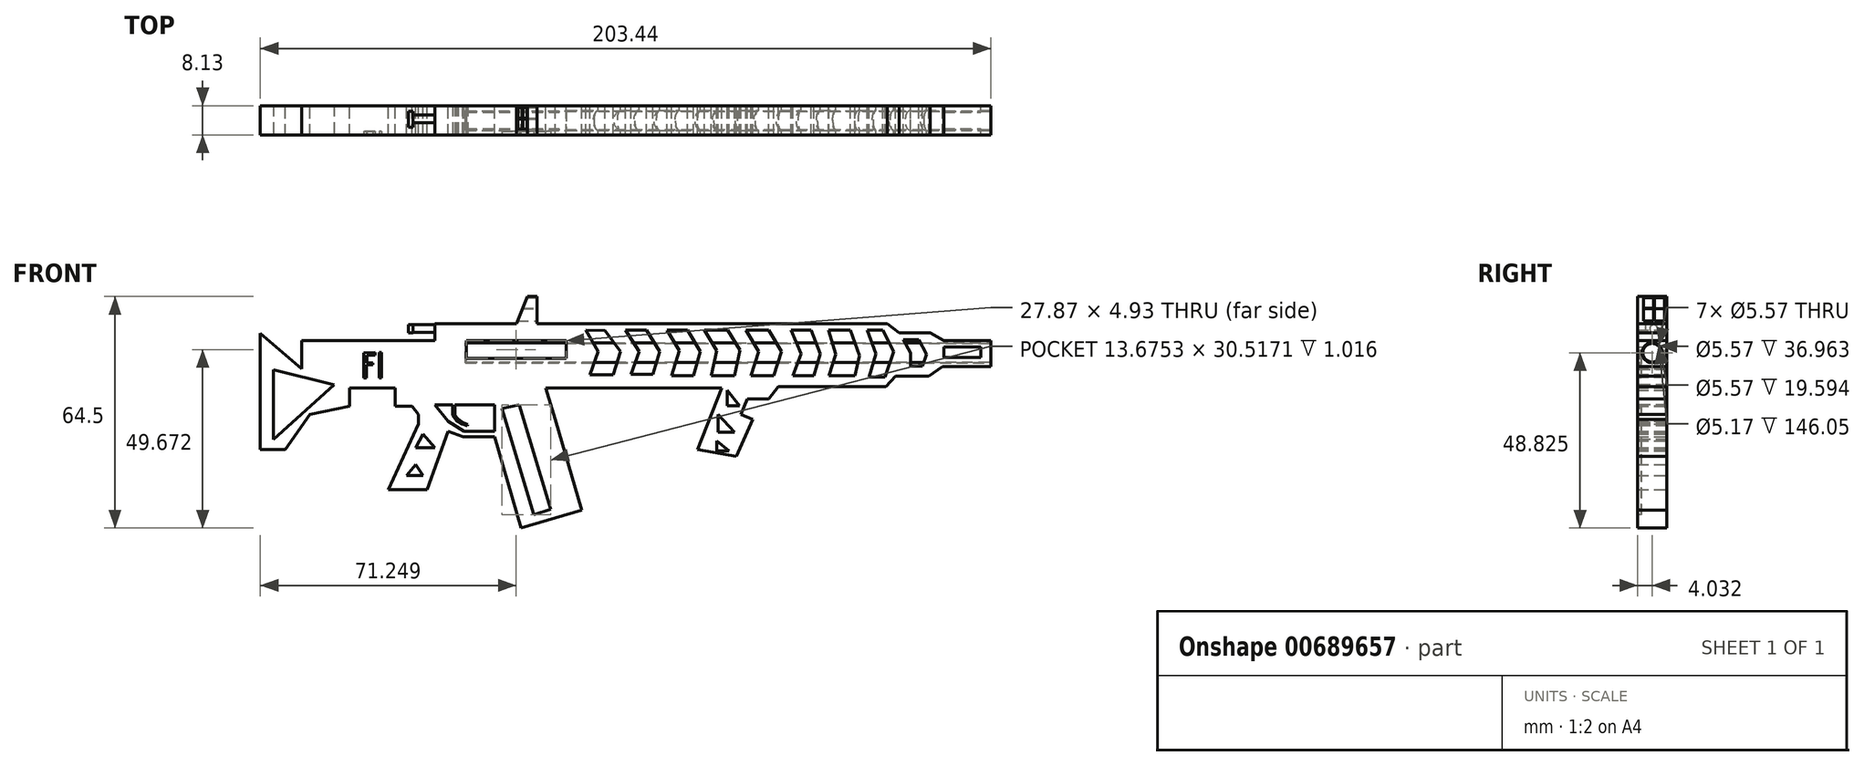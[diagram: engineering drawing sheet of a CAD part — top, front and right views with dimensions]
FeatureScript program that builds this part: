
annotation { "Feature Type Name" : "Feature", "Feature Type Description" : "" }
export const myFeature = defineFeature(function(context is Context, id is Id, definition is map)
    precondition{}
    {
        {
            var Q0;
            Q0=qCreatedBy(makeId("Front.planeOp"),FACE);
            var sketch = newSketch(context, id + "F0", { "sketchPlane" : qUnion([Q0])});
            skLineSegment(sketch, "E0", {"start": v(-48.63, 33.27) * mm, "end": v(-48.63, 11.1) * mm});
            skLineSegment(sketch, "E1", {"start": v(-48.63, 11.1) * mm, "end": v(-41.62, 11.1) * mm});
            skLineSegment(sketch, "E2", {"start": v(-41.62, 11.1) * mm, "end": v(-34.8, 20.95) * mm});
            skLineSegment(sketch, "E3", {"start": v(-34.8, 20.95) * mm, "end": v(-23.8, 23.23) * mm});
            skLineSegment(sketch, "E4", {"start": v(-23.8, 23.23) * mm, "end": v(-23.8, 28.34) * mm});
            skLineSegment(sketch, "E5", {"start": v(-23.8, 28.34) * mm, "end": v(-11.1, 28.34) * mm});
            skLineSegment(sketch, "E6", {"start": v(-11.1, 28.34) * mm, "end": v(-11.1, 23.23) * mm});
            skLineSegment(sketch, "E7", {"start": v(-11.1, 23.23) * mm, "end": v(-6.35, 23.23) * mm});
            skLineSegment(sketch, "E8", {"start": v(-6.35, 23.23) * mm, "end": v(-4.65, 20.95) * mm});
            skLineSegment(sketch, "E9", {"start": v(-4.65, 20.95) * mm, "end": v(-4.65, 18.3) * mm});
            skLineSegment(sketch, "E10", {"start": v(-4.65, 18.3) * mm, "end": v(-12.99, 0) * mm});
            skLineSegment(sketch, "E11", {"start": v(-12.99, 0) * mm, "end": v(-2.18, 0) * mm});
            skLineSegment(sketch, "E12", {"start": v(-2.18, 0) * mm, "end": v(3.7, 16.21) * mm});
            skLineSegment(sketch, "E13", {"start": v(3.7, 16.21) * mm, "end": v(7.92, 14.68) * mm});
            skLineSegment(sketch, "E14", {"start": v(7.92, 14.68) * mm, "end": v(16.59, 14.68) * mm});
            skLineSegment(sketch, "E15", {"start": v(16.59, 14.68) * mm, "end": v(23.98, -10.71) * mm});
            skLineSegment(sketch, "E16", {"start": v(23.98, -10.71) * mm, "end": v(40.91, -5.78) * mm});
            skLineSegment(sketch, "E17", {"start": v(40.91, -5.78) * mm, "end": v(33.55, 19.5) * mm});
            skLineSegment(sketch, "E18", {"start": v(33.55, 19.5) * mm, "end": v(30.8, 28.34) * mm});
            skLineSegment(sketch, "E19", {"start": v(30.8, 28.34) * mm, "end": v(79.92, 28.34) * mm});
            skLineSegment(sketch, "E20", {"start": v(79.92, 28.34) * mm, "end": v(73.09, 11.1) * mm});
            skLineSegment(sketch, "E21", {"start": v(73.09, 11.1) * mm, "end": v(83.9, 9.2) * mm});
            skLineSegment(sketch, "E22", {"start": v(83.9, 9.2) * mm, "end": v(88.45, 19.5) * mm});
            skLineSegment(sketch, "E23", {"start": v(88.45, 19.5) * mm, "end": v(85.15, 20.95) * mm});
            skLineSegment(sketch, "E24", {"start": v(85.15, 20.95) * mm, "end": v(87.03, 25.22) * mm});
            skLineSegment(sketch, "E25", {"start": v(87.03, 25.22) * mm, "end": v(93, 25.22) * mm});
            skLineSegment(sketch, "E26", {"start": v(93, 25.22) * mm, "end": v(95.65, 28.72) * mm});
            skLineSegment(sketch, "E27", {"start": v(95.65, 28.72) * mm, "end": v(125.6, 28.72) * mm});
            skLineSegment(sketch, "E28", {"start": v(125.6, 28.72) * mm, "end": v(128.26, 31.57) * mm});
            skLineSegment(sketch, "E29", {"start": v(128.26, 31.57) * mm, "end": v(137.55, 31.57) * mm});
            skLineSegment(sketch, "E30", {"start": v(137.55, 31.57) * mm, "end": v(141.34, 34.22) * mm});
            skLineSegment(sketch, "E31", {"start": v(141.34, 34.22) * mm, "end": v(154.8, 34.22) * mm});
            skLineSegment(sketch, "E32", {"start": v(154.8, 34.22) * mm, "end": v(154.8, 39.34) * mm});
            skLineSegment(sketch, "E33", {"start": v(154.8, 39.34) * mm, "end": v(154.8, 41.43) * mm});
            skLineSegment(sketch, "E34", {"start": v(154.8, 41.43) * mm, "end": v(141.72, 41.43) * mm});
            skLineSegment(sketch, "E35", {"start": v(141.72, 41.43) * mm, "end": v(137.93, 43.7) * mm});
            skLineSegment(sketch, "E36", {"start": v(137.93, 43.7) * mm, "end": v(129.21, 43.7) * mm});
            skLineSegment(sketch, "E37", {"start": v(129.21, 43.7) * mm, "end": v(125.92, 46.17) * mm});
            skLineSegment(sketch, "E38", {"start": v(125.92, 46.17) * mm, "end": v(0, 46.17) * mm});
            skLineSegment(sketch, "E39", {"start": v(0, 46.17) * mm, "end": v(0, 41.43) * mm});
            skLineSegment(sketch, "E40", {"start": v(0, 41.43) * mm, "end": v(-37.07, 41.43) * mm});
            skLineSegment(sketch, "E41", {"start": v(-37.07, 41.43) * mm, "end": v(-37.07, 33.65) * mm});
            skLineSegment(sketch, "E42", {"start": v(-48.63, 33.27) * mm, "end": v(-48.63, 43.51) * mm});
            skLineSegment(sketch, "E43", {"start": v(-48.63, 43.51) * mm, "end": v(-37.07, 33.65) * mm});
            skLineSegment(sketch, "E44", {"start": v(-3.32, 15.45) * mm, "end": v(-5.4, 11.66) * mm});
            skLineSegment(sketch, "E45", {"start": v(-5.4, 11.66) * mm, "end": v(0, 11.66) * mm});
            skLineSegment(sketch, "E46", {"start": v(0, 11.66) * mm, "end": v(-3.32, 15.45) * mm});
            skLineSegment(sketch, "E47", {"start": v(-5.4, 6.92) * mm, "end": v(-7.87, 3.89) * mm});
            skLineSegment(sketch, "E48", {"start": v(-7.87, 3.89) * mm, "end": v(-3.32, 3.89) * mm});
            skLineSegment(sketch, "E49", {"start": v(-3.32, 3.89) * mm, "end": v(-5.4, 6.92) * mm});
            skLineSegment(sketch, "E50", {"start": v(3.7, 19.05) * mm, "end": v(8.06, 16.21) * mm});
            skLineSegment(sketch, "E51", {"start": v(8.06, 16.21) * mm, "end": v(16.59, 16.21) * mm});
            skLineSegment(sketch, "E52", {"start": v(16.59, 16.21) * mm, "end": v(16.59, 23.6) * mm});
            skLineSegment(sketch, "E53", {"start": v(16.59, 23.6) * mm, "end": v(0, 23.6) * mm});
            skLineSegment(sketch, "E54", {"start": v(0, 23.6) * mm, "end": v(3.7, 19.05) * mm});
            skLineSegment(sketch, "E55", {"start": v(6.35, 23.6) * mm, "end": v(6.35, 20.95) * mm});
            skLineSegment(sketch, "E56", {"start": v(6.35, 20.95) * mm, "end": v(7.68, 19.05) * mm});
            skLineSegment(sketch, "E57", {"start": v(7.68, 19.05) * mm, "end": v(9.32, 17.46) * mm});
            skLineSegment(sketch, "E58", {"start": v(9.32, 17.46) * mm, "end": v(9.77, 17.92) * mm});
            skLineSegment(sketch, "E59", {"start": v(9.77, 17.92) * mm, "end": v(8.6, 19.05) * mm});
            skLineSegment(sketch, "E60", {"start": v(8.6, 19.05) * mm, "end": v(7.08, 20.95) * mm});
            skLineSegment(sketch, "E61", {"start": v(7.08, 20.95) * mm, "end": v(7.08, 23.6) * mm});
            skLineSegment(sketch, "E62", {"start": v(7.08, 23.6) * mm, "end": v(6.35, 23.6) * mm});
            skLineSegment(sketch, "E63", {"start": v(42.05, 44.46) * mm, "end": v(45.46, 38.4) * mm});
            skLineSegment(sketch, "E64", {"start": v(45.46, 38.4) * mm, "end": v(43.19, 31.95) * mm});
            skLineSegment(sketch, "E65", {"start": v(43.19, 31.95) * mm, "end": v(49.64, 31.95) * mm});
            skLineSegment(sketch, "E66", {"start": v(49.64, 31.95) * mm, "end": v(51.72, 38.4) * mm});
            skLineSegment(sketch, "E67", {"start": v(51.72, 38.4) * mm, "end": v(47.36, 44.27) * mm});
            skLineSegment(sketch, "E68", {"start": v(47.36, 44.27) * mm, "end": v(42.05, 44.46) * mm});
            skLineSegment(sketch, "E69", {"start": v(53.05, 44.46) * mm, "end": v(56.84, 38.4) * mm});
            skLineSegment(sketch, "E70", {"start": v(56.84, 38.4) * mm, "end": v(54.57, 32.14) * mm});
            skLineSegment(sketch, "E71", {"start": v(54.57, 32.14) * mm, "end": v(60.63, 32.14) * mm});
            skLineSegment(sketch, "E72", {"start": v(60.63, 32.14) * mm, "end": v(62.53, 38.4) * mm});
            skLineSegment(sketch, "E73", {"start": v(62.53, 38.4) * mm, "end": v(58.93, 44.46) * mm});
            skLineSegment(sketch, "E74", {"start": v(58.93, 44.46) * mm, "end": v(53.05, 44.46) * mm});
            skLineSegment(sketch, "E75", {"start": v(64.61, 44.46) * mm, "end": v(68.07, 38.64) * mm});
            skLineSegment(sketch, "E76", {"start": v(68.07, 38.64) * mm, "end": v(65.94, 31.76) * mm});
            skLineSegment(sketch, "E77", {"start": v(65.94, 31.76) * mm, "end": v(72, 31.76) * mm});
            skLineSegment(sketch, "E78", {"start": v(72, 31.76) * mm, "end": v(73.9, 38.4) * mm});
            skLineSegment(sketch, "E79", {"start": v(73.9, 38.4) * mm, "end": v(70.3, 44.46) * mm});
            skLineSegment(sketch, "E80", {"start": v(70.3, 44.46) * mm, "end": v(64.61, 44.46) * mm});
            skLineSegment(sketch, "E81", {"start": v(75.04, 44.46) * mm, "end": v(78.5, 38.64) * mm});
            skLineSegment(sketch, "E82", {"start": v(78.5, 38.64) * mm, "end": v(76.94, 31.76) * mm});
            skLineSegment(sketch, "E83", {"start": v(76.94, 31.76) * mm, "end": v(83.38, 31.76) * mm});
            skLineSegment(sketch, "E84", {"start": v(83.38, 31.76) * mm, "end": v(84.9, 38.77) * mm});
            skLineSegment(sketch, "E85", {"start": v(84.9, 38.77) * mm, "end": v(81.52, 44.46) * mm});
            skLineSegment(sketch, "E86", {"start": v(75.04, 44.46) * mm, "end": v(81.52, 44.46) * mm});
            skLineSegment(sketch, "E87", {"start": v(86.6, 44.46) * mm, "end": v(90.2, 38.4) * mm});
            skLineSegment(sketch, "E88", {"start": v(90.2, 38.4) * mm, "end": v(88.03, 31.66) * mm});
            skLineSegment(sketch, "E89", {"start": v(88.03, 31.66) * mm, "end": v(94.38, 31.66) * mm});
            skLineSegment(sketch, "E90", {"start": v(94.38, 31.66) * mm, "end": v(96.56, 38.4) * mm});
            skLineSegment(sketch, "E91", {"start": v(96.56, 38.4) * mm, "end": v(92.96, 44.46) * mm});
            skLineSegment(sketch, "E92", {"start": v(92.96, 44.46) * mm, "end": v(86.6, 44.46) * mm});
            skLineSegment(sketch, "E93", {"start": v(99.69, 31.66) * mm, "end": v(101.96, 37.82) * mm});
            skLineSegment(sketch, "E94", {"start": v(101.96, 37.82) * mm, "end": v(99.12, 44.46) * mm});
            skLineSegment(sketch, "E95", {"start": v(99.12, 44.46) * mm, "end": v(104.8, 44.46) * mm});
            skLineSegment(sketch, "E96", {"start": v(104.8, 44.46) * mm, "end": v(107.27, 37.82) * mm});
            skLineSegment(sketch, "E97", {"start": v(107.27, 37.82) * mm, "end": v(105.57, 31.66) * mm});
            skLineSegment(sketch, "E98", {"start": v(105.57, 31.66) * mm, "end": v(99.69, 31.66) * mm});
            skLineSegment(sketch, "E99", {"start": v(109.55, 44.46) * mm, "end": v(111.63, 37.64) * mm});
            skLineSegment(sketch, "E100", {"start": v(111.63, 37.64) * mm, "end": v(109.74, 31.66) * mm});
            skLineSegment(sketch, "E101", {"start": v(109.74, 31.66) * mm, "end": v(116.94, 31.66) * mm});
            skLineSegment(sketch, "E102", {"start": v(116.94, 31.66) * mm, "end": v(118.27, 37.26) * mm});
            skLineSegment(sketch, "E103", {"start": v(118.27, 37.26) * mm, "end": v(115.62, 44.46) * mm});
            skLineSegment(sketch, "E104", {"start": v(115.62, 44.46) * mm, "end": v(109.55, 44.46) * mm});
            skLineSegment(sketch, "E105", {"start": v(120.36, 44.46) * mm, "end": v(122.82, 37.82) * mm});
            skPoint(sketch, "E105.startSnap0", {"position": v(112.58, 44.46) * mm});
            skLineSegment(sketch, "E106", {"start": v(122.82, 37.82) * mm, "end": v(120.92, 31.38) * mm});
            skLineSegment(sketch, "E107", {"start": v(120.92, 31.38) * mm, "end": v(125.29, 31.38) * mm});
            skLineSegment(sketch, "E108", {"start": v(125.29, 31.38) * mm, "end": v(127.75, 38.4) * mm});
            skLineSegment(sketch, "E109", {"start": v(127.75, 38.4) * mm, "end": v(124.72, 44.46) * mm});
            skLineSegment(sketch, "E110", {"start": v(124.72, 44.46) * mm, "end": v(120.36, 44.46) * mm});
            skLineSegment(sketch, "E111", {"start": v(130.4, 41.8) * mm, "end": v(132.5, 38.01) * mm});
            skLineSegment(sketch, "E112", {"start": v(132.5, 38.01) * mm, "end": v(132.5, 34.41) * mm});
            skLineSegment(sketch, "E113", {"start": v(132.5, 34.41) * mm, "end": v(135.78, 34.41) * mm});
            skLineSegment(sketch, "E114", {"start": v(135.78, 34.41) * mm, "end": v(136.85, 37.64) * mm});
            skLineSegment(sketch, "E115", {"start": v(136.85, 37.64) * mm, "end": v(134.77, 41.8) * mm});
            skLineSegment(sketch, "E116", {"start": v(134.77, 41.8) * mm, "end": v(130.4, 41.8) * mm});
            skLineSegment(sketch, "E117", {"start": v(141.72, 39.72) * mm, "end": v(141.72, 36.78) * mm});
            skPoint(sketch, "E117.endSnap0", {"position": v(154.8, 36.78) * mm});
            skLineSegment(sketch, "E118", {"start": v(141.72, 36.78) * mm, "end": v(152.02, 36.78) * mm});
            skLineSegment(sketch, "E119", {"start": v(152.02, 36.78) * mm, "end": v(152.02, 39.72) * mm});
            skLineSegment(sketch, "E120", {"start": v(152.02, 39.72) * mm, "end": v(141.72, 39.72) * mm});
            skLineSegment(sketch, "E121.bottom", {"start": v(8.68, 41.43) * mm, "end": v(36.55, 41.43) * mm});
            skLineSegment(sketch, "E121.top", {"start": v(8.68, 36.5) * mm, "end": v(36.55, 36.5) * mm});
            skLineSegment(sketch, "E121.left", {"start": v(8.68, 41.43) * mm, "end": v(8.68, 36.5) * mm});
            skLineSegment(sketch, "E121.right", {"start": v(36.55, 41.43) * mm, "end": v(36.55, 36.5) * mm});
            skLineSegment(sketch, "E122", {"start": v(78.83, 20.95) * mm, "end": v(78.83, 16.02) * mm});
            skLineSegment(sketch, "E123", {"start": v(78.83, 16.02) * mm, "end": v(83.38, 16.02) * mm});
            skLineSegment(sketch, "E124", {"start": v(83.38, 16.02) * mm, "end": v(78.83, 20.95) * mm});
            skLineSegment(sketch, "E125", {"start": v(78.5, 13.56) * mm, "end": v(78.5, 10.71) * mm});
            skPoint(sketch, "E125.startSnap0", {"position": v(78.5, 10.14) * mm});
            skLineSegment(sketch, "E126", {"start": v(78.5, 10.71) * mm, "end": v(81.9, 10.71) * mm});
            skLineSegment(sketch, "E127", {"start": v(81.9, 10.71) * mm, "end": v(78.5, 13.56) * mm});
            skLineSegment(sketch, "E128", {"start": v(81.34, 27.67) * mm, "end": v(81.34, 23.31) * mm});
            skLineSegment(sketch, "E129", {"start": v(81.34, 23.31) * mm, "end": v(84.86, 23.31) * mm});
            skLineSegment(sketch, "E130", {"start": v(84.86, 23.31) * mm, "end": v(81.34, 27.67) * mm});
            skSolve(sketch);
        }
        {
            var Q0;
            Q0=makeQuery(id+"F0.imprint","IMPRINT",FACE,{"disambiguationData":[TD([[makeQuery(id+"F0.imprint","IMPRINT",EDGE,{"derivedFrom":sQuery(id+"F0.wireOp",EDGE,"E0")}),1.0]])]});
            extrude(context, id + "F1", {"entities" : qUnion([Q0]), "depth" : 7.62 * mm, "offsetDistance" : 25.4 * mm});
        }
        {
            var Q0;
            Q0=makeQuery(id+"F1.opExtrude","SWEPT_FACE",FACE,{"disambiguationData":[OSD([sQuery(id+"F0.wireOp",EDGE,"E32"),sQuery(id+"F0.wireOp",EDGE,"E33")])]});
            var sketch = newSketch(context, id + "F2", { "sketchPlane" : qUnion([Q0])});
            skCircle(sketch, "E131", {"center": v(-4.1, 38.11) * mm, "radius": 2.79 * mm});
            skSolve(sketch);
        }
        {
            var Q0;
            Q0 = qSketchRegion(id + "F2", true);
            extrude(context, id + "F3", {"entities" : qUnion([Q0]), "operationType" : NewBodyOperationType.REMOVE, "oppositeDirection" : true, "depth" : 146.3 * mm, "offsetDistance" : 25.4 * mm});
        }
        {
            var Q0;
            Q0=makeQuery(id+"F1.opExtrude","SWEPT_FACE",FACE,{"disambiguationData":[OSD([sQuery(id+"F0.wireOp",EDGE,"E32"),sQuery(id+"F0.wireOp",EDGE,"E33")])]});
            var sketch = newSketch(context, id + "F4", { "sketchPlane" : qUnion([Q0])});
            skCircle(sketch, "E132", {"center": v(-4.1, 38.11) * mm, "radius": 2.72 * mm});
            skSolve(sketch);
        }
        {
            var Q0;
            Q0 = qSketchRegion(id + "F4", true);
            extrude(context, id + "F5", {"entities" : qUnion([Q0]), "operationType" : NewBodyOperationType.ADD, "oppositeDirection" : true, "depth" : 146.8 * mm, "offsetDistance" : 25.4 * mm});
        }
        {
            var Q0;
            Q0=makeQuery(id+"F5.opExtrude","CAP_FACE",FACE,{"disambiguationData":[OSD([sQuery(id+"F4.wireOp",EDGE,"E132")])],"isStart":true});
            var sketch = newSketch(context, id + "F6", { "sketchPlane" : qUnion([Q0])});
            skCircle(sketch, "E133", {"center": v(-4.1, 38.11) * mm, "radius": 2.59 * mm});
            skSolve(sketch);
        }
        {
            var Q0;
            Q0 = qSketchRegion(id + "F6", true);
            extrude(context, id + "F7", {"entities" : qUnion([Q0]), "operationType" : NewBodyOperationType.REMOVE, "oppositeDirection" : true, "depth" : 146.05 * mm, "offsetDistance" : 25.4 * mm});
        }
        {
            var Q0;
            Q0=makeQuery(id+"F1.opExtrude","SWEPT_FACE",FACE,{"disambiguationData":[OSD([sQuery(id+"F0.wireOp",EDGE,"E38")])]});
            var sketch = newSketch(context, id + "F8", { "sketchPlane" : qUnion([Q0])});
            skLineSegment(sketch, "E134", {"start": v(15.89, 0) * mm, "end": v(15.89, -7.62) * mm});
            skLineSegment(sketch, "E135", {"start": v(15.89, -7.62) * mm, "end": v(28.4, -7.62) * mm});
            skLineSegment(sketch, "E136", {"start": v(28.4, -7.62) * mm, "end": v(28.4, 0) * mm});
            skLineSegment(sketch, "E137", {"start": v(28.4, 0) * mm, "end": v(15.89, 0) * mm});
            skSolve(sketch);
        }
        {
            var Q0;
            Q0 = qSketchRegion(id + "F8", true);
            extrude(context, id + "F9", {"entities" : qUnion([Q0]), "operationType" : NewBodyOperationType.ADD, "depth" : 7.62 * mm, "offsetDistance" : 25.4 * mm});
        }
        {
            var Q0;
            Q0=makeQuery(id+"F9.boolean.opBoolean","MERGE",FACE,{"derivedFrom":[makeQuery(id+"F1.opExtrude","CAP_FACE",FACE,{"disambiguationData":[OSD([sQuery(id+"F0.wireOp",EDGE,"E0"),sQuery(id+"F0.wireOp",EDGE,"E1"),sQuery(id+"F0.wireOp",EDGE,"E2"),sQuery(id+"F0.wireOp",EDGE,"E3"),sQuery(id+"F0.wireOp",EDGE,"E4"),sQuery(id+"F0.wireOp",EDGE,"E5"),sQuery(id+"F0.wireOp",EDGE,"E6"),sQuery(id+"F0.wireOp",EDGE,"E7"),sQuery(id+"F0.wireOp",EDGE,"E8"),sQuery(id+"F0.wireOp",EDGE,"E9"),sQuery(id+"F0.wireOp",EDGE,"E10"),sQuery(id+"F0.wireOp",EDGE,"E11"),sQuery(id+"F0.wireOp",EDGE,"E12"),sQuery(id+"F0.wireOp",EDGE,"E13"),sQuery(id+"F0.wireOp",EDGE,"E14"),sQuery(id+"F0.wireOp",EDGE,"E15"),sQuery(id+"F0.wireOp",EDGE,"E16"),sQuery(id+"F0.wireOp",EDGE,"E17"),sQuery(id+"F0.wireOp",EDGE,"E18"),sQuery(id+"F0.wireOp",EDGE,"E19"),sQuery(id+"F0.wireOp",EDGE,"E20"),sQuery(id+"F0.wireOp",EDGE,"E21"),sQuery(id+"F0.wireOp",EDGE,"E22"),sQuery(id+"F0.wireOp",EDGE,"E23"),sQuery(id+"F0.wireOp",EDGE,"E24"),sQuery(id+"F0.wireOp",EDGE,"E25"),sQuery(id+"F0.wireOp",EDGE,"E26"),sQuery(id+"F0.wireOp",EDGE,"E27"),sQuery(id+"F0.wireOp",EDGE,"E28"),sQuery(id+"F0.wireOp",EDGE,"E29"),sQuery(id+"F0.wireOp",EDGE,"E30"),sQuery(id+"F0.wireOp",EDGE,"E31"),sQuery(id+"F0.wireOp",EDGE,"E32"),sQuery(id+"F0.wireOp",EDGE,"E33"),sQuery(id+"F0.wireOp",EDGE,"E34"),sQuery(id+"F0.wireOp",EDGE,"E35"),sQuery(id+"F0.wireOp",EDGE,"E36"),sQuery(id+"F0.wireOp",EDGE,"E37"),sQuery(id+"F0.wireOp",EDGE,"E38"),sQuery(id+"F0.wireOp",EDGE,"E39"),sQuery(id+"F0.wireOp",EDGE,"E40"),sQuery(id+"F0.wireOp",EDGE,"E41"),sQuery(id+"F0.wireOp",EDGE,"E42"),sQuery(id+"F0.wireOp",EDGE,"E43"),sQuery(id+"F0.wireOp",EDGE,"E44"),sQuery(id+"F0.wireOp",EDGE,"E45"),sQuery(id+"F0.wireOp",EDGE,"E46"),sQuery(id+"F0.wireOp",EDGE,"E47"),sQuery(id+"F0.wireOp",EDGE,"E48"),sQuery(id+"F0.wireOp",EDGE,"E49"),sQuery(id+"F0.wireOp",EDGE,"E50"),sQuery(id+"F0.wireOp",EDGE,"E51"),sQuery(id+"F0.wireOp",EDGE,"E52"),sQuery(id+"F0.wireOp",EDGE,"E53"),sQuery(id+"F0.wireOp",EDGE,"E54"),sQuery(id+"F0.wireOp",EDGE,"E62"),sQuery(id+"F0.wireOp",EDGE,"E63"),sQuery(id+"F0.wireOp",EDGE,"E64"),sQuery(id+"F0.wireOp",EDGE,"E65"),sQuery(id+"F0.wireOp",EDGE,"E66"),sQuery(id+"F0.wireOp",EDGE,"E67"),sQuery(id+"F0.wireOp",EDGE,"E68"),sQuery(id+"F0.wireOp",EDGE,"E69"),sQuery(id+"F0.wireOp",EDGE,"E70"),sQuery(id+"F0.wireOp",EDGE,"E71"),sQuery(id+"F0.wireOp",EDGE,"E72"),sQuery(id+"F0.wireOp",EDGE,"E73"),sQuery(id+"F0.wireOp",EDGE,"E74"),sQuery(id+"F0.wireOp",EDGE,"E75"),sQuery(id+"F0.wireOp",EDGE,"E76"),sQuery(id+"F0.wireOp",EDGE,"E77"),sQuery(id+"F0.wireOp",EDGE,"E78"),sQuery(id+"F0.wireOp",EDGE,"E79"),sQuery(id+"F0.wireOp",EDGE,"E80"),sQuery(id+"F0.wireOp",EDGE,"E81"),sQuery(id+"F0.wireOp",EDGE,"E82"),sQuery(id+"F0.wireOp",EDGE,"E83"),sQuery(id+"F0.wireOp",EDGE,"E84"),sQuery(id+"F0.wireOp",EDGE,"E85"),sQuery(id+"F0.wireOp",EDGE,"E86"),sQuery(id+"F0.wireOp",EDGE,"E87"),sQuery(id+"F0.wireOp",EDGE,"E88"),sQuery(id+"F0.wireOp",EDGE,"E89"),sQuery(id+"F0.wireOp",EDGE,"E90"),sQuery(id+"F0.wireOp",EDGE,"E91"),sQuery(id+"F0.wireOp",EDGE,"E92"),sQuery(id+"F0.wireOp",EDGE,"E93"),sQuery(id+"F0.wireOp",EDGE,"E94"),sQuery(id+"F0.wireOp",EDGE,"E95"),sQuery(id+"F0.wireOp",EDGE,"E96"),sQuery(id+"F0.wireOp",EDGE,"E97"),sQuery(id+"F0.wireOp",EDGE,"E98"),sQuery(id+"F0.wireOp",EDGE,"E99"),sQuery(id+"F0.wireOp",EDGE,"E100"),sQuery(id+"F0.wireOp",EDGE,"E101"),sQuery(id+"F0.wireOp",EDGE,"E102"),sQuery(id+"F0.wireOp",EDGE,"E103"),sQuery(id+"F0.wireOp",EDGE,"E104"),sQuery(id+"F0.wireOp",EDGE,"E105"),sQuery(id+"F0.wireOp",EDGE,"E106"),sQuery(id+"F0.wireOp",EDGE,"E107"),sQuery(id+"F0.wireOp",EDGE,"E108"),sQuery(id+"F0.wireOp",EDGE,"E109"),sQuery(id+"F0.wireOp",EDGE,"E110"),sQuery(id+"F0.wireOp",EDGE,"E111"),sQuery(id+"F0.wireOp",EDGE,"E112"),sQuery(id+"F0.wireOp",EDGE,"E113"),sQuery(id+"F0.wireOp",EDGE,"E114"),sQuery(id+"F0.wireOp",EDGE,"E115"),sQuery(id+"F0.wireOp",EDGE,"E116"),sQuery(id+"F0.wireOp",EDGE,"E117"),sQuery(id+"F0.wireOp",EDGE,"E118"),sQuery(id+"F0.wireOp",EDGE,"E119"),sQuery(id+"F0.wireOp",EDGE,"E120"),sQuery(id+"F0.wireOp",EDGE,"E121.bottom"),sQuery(id+"F0.wireOp",EDGE,"E121.top"),sQuery(id+"F0.wireOp",EDGE,"E121.left"),sQuery(id+"F0.wireOp",EDGE,"E121.right"),sQuery(id+"F0.wireOp",EDGE,"E122"),sQuery(id+"F0.wireOp",EDGE,"E123"),sQuery(id+"F0.wireOp",EDGE,"E124"),sQuery(id+"F0.wireOp",EDGE,"E125"),sQuery(id+"F0.wireOp",EDGE,"E126"),sQuery(id+"F0.wireOp",EDGE,"E127"),sQuery(id+"F0.wireOp",EDGE,"E128"),sQuery(id+"F0.wireOp",EDGE,"E129"),sQuery(id+"F0.wireOp",EDGE,"E130")])],"isStart":false}),makeQuery(id+"F9.opExtrude","SWEPT_FACE",FACE,{"disambiguationData":[OSD([sQuery(id+"F8.wireOp",EDGE,"E135")])]})]});
            var sketch = newSketch(context, id + "F10", { "sketchPlane" : qUnion([Q0])});
            skLineSegment(sketch, "E138", {"start": v(15.89, 46.17) * mm, "end": v(22.72, 46.17) * mm});
            skLineSegment(sketch, "E139", {"start": v(22.72, 46.17) * mm, "end": v(25.8, 53.79) * mm});
            skLineSegment(sketch, "E140", {"start": v(25.8, 53.79) * mm, "end": v(15.89, 53.79) * mm});
            skLineSegment(sketch, "E141", {"start": v(15.89, 53.79) * mm, "end": v(15.89, 46.17) * mm});
            skSolve(sketch);
        }
        {
            var Q0;
            Q0 = qSketchRegion(id + "F10", true);
            extrude(context, id + "F11", {"entities" : qUnion([Q0]), "operationType" : NewBodyOperationType.REMOVE, "oppositeDirection" : true, "depth" : 25.4 * mm, "offsetDistance" : 25.4 * mm});
        }
        {
            var Q0;
            Q0=makeQuery(id+"F9.opExtrude","SWEPT_FACE",FACE,{"disambiguationData":[OSD([sQuery(id+"F8.wireOp",EDGE,"E136")])]});
            var sketch = newSketch(context, id + "F12", { "sketchPlane" : qUnion([Q0])});
            skLineSegment(sketch, "E142", {"start": v(-6.51, 53.46) * mm, "end": v(-6.51, 50.45) * mm});
            skLineSegment(sketch, "E143", {"start": v(-6.51, 50.45) * mm, "end": v(-3.67, 50.45) * mm});
            skLineSegment(sketch, "E144", {"start": v(-3.67, 50.45) * mm, "end": v(-3.67, 53.47) * mm});
            skLineSegment(sketch, "E145", {"start": v(-3.67, 53.47) * mm, "end": v(-6.51, 53.46) * mm});
            skLineSegment(sketch, "E146", {"start": v(-3.48, 53.46) * mm, "end": v(-0.59, 53.47) * mm});
            skLineSegment(sketch, "E147", {"start": v(-0.59, 53.47) * mm, "end": v(-0.59, 50.45) * mm});
            skLineSegment(sketch, "E148", {"start": v(-0.59, 50.45) * mm, "end": v(-3.48, 50.43) * mm});
            skLineSegment(sketch, "E149", {"start": v(-3.48, 50.43) * mm, "end": v(-3.48, 53.46) * mm});
            skLineSegment(sketch, "E150", {"start": v(-6.52, 50.32) * mm, "end": v(-6.52, 46.98) * mm});
            skLineSegment(sketch, "E151", {"start": v(-6.52, 46.98) * mm, "end": v(-3.67, 46.98) * mm});
            skLineSegment(sketch, "E152", {"start": v(-3.67, 46.98) * mm, "end": v(-3.67, 50.32) * mm});
            skLineSegment(sketch, "E153", {"start": v(-3.67, 50.32) * mm, "end": v(-6.52, 50.32) * mm});
            skLineSegment(sketch, "E154", {"start": v(-3.48, 50.32) * mm, "end": v(-0.59, 50.32) * mm});
            skLineSegment(sketch, "E155", {"start": v(-0.59, 50.32) * mm, "end": v(-0.59, 46.98) * mm});
            skLineSegment(sketch, "E156", {"start": v(-0.59, 46.98) * mm, "end": v(-3.48, 46.98) * mm});
            skLineSegment(sketch, "E157", {"start": v(-3.48, 46.98) * mm, "end": v(-3.48, 50.32) * mm});
            skSolve(sketch);
        }
        {
            var Q0;
            Q0 = qSketchRegion(id + "F12", true);
            extrude(context, id + "F13", {"entities" : qUnion([Q0]), "operationType" : NewBodyOperationType.REMOVE, "oppositeDirection" : true, "depth" : 25.4 * mm, "offsetDistance" : 25.4 * mm});
        }
        {
            var Q0;
            Q0=makeQuery(id+"F9.boolean.opBoolean","MERGE",FACE,{"derivedFrom":[makeQuery(id+"F1.opExtrude","CAP_FACE",FACE,{"disambiguationData":[OSD([sQuery(id+"F0.wireOp",EDGE,"E0"),sQuery(id+"F0.wireOp",EDGE,"E1"),sQuery(id+"F0.wireOp",EDGE,"E2"),sQuery(id+"F0.wireOp",EDGE,"E3"),sQuery(id+"F0.wireOp",EDGE,"E4"),sQuery(id+"F0.wireOp",EDGE,"E5"),sQuery(id+"F0.wireOp",EDGE,"E6"),sQuery(id+"F0.wireOp",EDGE,"E7"),sQuery(id+"F0.wireOp",EDGE,"E8"),sQuery(id+"F0.wireOp",EDGE,"E9"),sQuery(id+"F0.wireOp",EDGE,"E10"),sQuery(id+"F0.wireOp",EDGE,"E11"),sQuery(id+"F0.wireOp",EDGE,"E12"),sQuery(id+"F0.wireOp",EDGE,"E13"),sQuery(id+"F0.wireOp",EDGE,"E14"),sQuery(id+"F0.wireOp",EDGE,"E15"),sQuery(id+"F0.wireOp",EDGE,"E16"),sQuery(id+"F0.wireOp",EDGE,"E17"),sQuery(id+"F0.wireOp",EDGE,"E18"),sQuery(id+"F0.wireOp",EDGE,"E19"),sQuery(id+"F0.wireOp",EDGE,"E20"),sQuery(id+"F0.wireOp",EDGE,"E21"),sQuery(id+"F0.wireOp",EDGE,"E22"),sQuery(id+"F0.wireOp",EDGE,"E23"),sQuery(id+"F0.wireOp",EDGE,"E24"),sQuery(id+"F0.wireOp",EDGE,"E25"),sQuery(id+"F0.wireOp",EDGE,"E26"),sQuery(id+"F0.wireOp",EDGE,"E27"),sQuery(id+"F0.wireOp",EDGE,"E28"),sQuery(id+"F0.wireOp",EDGE,"E29"),sQuery(id+"F0.wireOp",EDGE,"E30"),sQuery(id+"F0.wireOp",EDGE,"E31"),sQuery(id+"F0.wireOp",EDGE,"E32"),sQuery(id+"F0.wireOp",EDGE,"E33"),sQuery(id+"F0.wireOp",EDGE,"E34"),sQuery(id+"F0.wireOp",EDGE,"E35"),sQuery(id+"F0.wireOp",EDGE,"E36"),sQuery(id+"F0.wireOp",EDGE,"E37"),sQuery(id+"F0.wireOp",EDGE,"E38"),sQuery(id+"F0.wireOp",EDGE,"E39"),sQuery(id+"F0.wireOp",EDGE,"E40"),sQuery(id+"F0.wireOp",EDGE,"E41"),sQuery(id+"F0.wireOp",EDGE,"E42"),sQuery(id+"F0.wireOp",EDGE,"E43"),sQuery(id+"F0.wireOp",EDGE,"E44"),sQuery(id+"F0.wireOp",EDGE,"E45"),sQuery(id+"F0.wireOp",EDGE,"E46"),sQuery(id+"F0.wireOp",EDGE,"E47"),sQuery(id+"F0.wireOp",EDGE,"E48"),sQuery(id+"F0.wireOp",EDGE,"E49"),sQuery(id+"F0.wireOp",EDGE,"E50"),sQuery(id+"F0.wireOp",EDGE,"E51"),sQuery(id+"F0.wireOp",EDGE,"E52"),sQuery(id+"F0.wireOp",EDGE,"E53"),sQuery(id+"F0.wireOp",EDGE,"E54"),sQuery(id+"F0.wireOp",EDGE,"E62"),sQuery(id+"F0.wireOp",EDGE,"E63"),sQuery(id+"F0.wireOp",EDGE,"E64"),sQuery(id+"F0.wireOp",EDGE,"E65"),sQuery(id+"F0.wireOp",EDGE,"E66"),sQuery(id+"F0.wireOp",EDGE,"E67"),sQuery(id+"F0.wireOp",EDGE,"E68"),sQuery(id+"F0.wireOp",EDGE,"E69"),sQuery(id+"F0.wireOp",EDGE,"E70"),sQuery(id+"F0.wireOp",EDGE,"E71"),sQuery(id+"F0.wireOp",EDGE,"E72"),sQuery(id+"F0.wireOp",EDGE,"E73"),sQuery(id+"F0.wireOp",EDGE,"E74"),sQuery(id+"F0.wireOp",EDGE,"E75"),sQuery(id+"F0.wireOp",EDGE,"E76"),sQuery(id+"F0.wireOp",EDGE,"E77"),sQuery(id+"F0.wireOp",EDGE,"E78"),sQuery(id+"F0.wireOp",EDGE,"E79"),sQuery(id+"F0.wireOp",EDGE,"E80"),sQuery(id+"F0.wireOp",EDGE,"E81"),sQuery(id+"F0.wireOp",EDGE,"E82"),sQuery(id+"F0.wireOp",EDGE,"E83"),sQuery(id+"F0.wireOp",EDGE,"E84"),sQuery(id+"F0.wireOp",EDGE,"E85"),sQuery(id+"F0.wireOp",EDGE,"E86"),sQuery(id+"F0.wireOp",EDGE,"E87"),sQuery(id+"F0.wireOp",EDGE,"E88"),sQuery(id+"F0.wireOp",EDGE,"E89"),sQuery(id+"F0.wireOp",EDGE,"E90"),sQuery(id+"F0.wireOp",EDGE,"E91"),sQuery(id+"F0.wireOp",EDGE,"E92"),sQuery(id+"F0.wireOp",EDGE,"E93"),sQuery(id+"F0.wireOp",EDGE,"E94"),sQuery(id+"F0.wireOp",EDGE,"E95"),sQuery(id+"F0.wireOp",EDGE,"E96"),sQuery(id+"F0.wireOp",EDGE,"E97"),sQuery(id+"F0.wireOp",EDGE,"E98"),sQuery(id+"F0.wireOp",EDGE,"E99"),sQuery(id+"F0.wireOp",EDGE,"E100"),sQuery(id+"F0.wireOp",EDGE,"E101"),sQuery(id+"F0.wireOp",EDGE,"E102"),sQuery(id+"F0.wireOp",EDGE,"E103"),sQuery(id+"F0.wireOp",EDGE,"E104"),sQuery(id+"F0.wireOp",EDGE,"E105"),sQuery(id+"F0.wireOp",EDGE,"E106"),sQuery(id+"F0.wireOp",EDGE,"E107"),sQuery(id+"F0.wireOp",EDGE,"E108"),sQuery(id+"F0.wireOp",EDGE,"E109"),sQuery(id+"F0.wireOp",EDGE,"E110"),sQuery(id+"F0.wireOp",EDGE,"E111"),sQuery(id+"F0.wireOp",EDGE,"E112"),sQuery(id+"F0.wireOp",EDGE,"E113"),sQuery(id+"F0.wireOp",EDGE,"E114"),sQuery(id+"F0.wireOp",EDGE,"E115"),sQuery(id+"F0.wireOp",EDGE,"E116"),sQuery(id+"F0.wireOp",EDGE,"E117"),sQuery(id+"F0.wireOp",EDGE,"E118"),sQuery(id+"F0.wireOp",EDGE,"E119"),sQuery(id+"F0.wireOp",EDGE,"E120"),sQuery(id+"F0.wireOp",EDGE,"E121.bottom"),sQuery(id+"F0.wireOp",EDGE,"E121.top"),sQuery(id+"F0.wireOp",EDGE,"E121.left"),sQuery(id+"F0.wireOp",EDGE,"E121.right"),sQuery(id+"F0.wireOp",EDGE,"E122"),sQuery(id+"F0.wireOp",EDGE,"E123"),sQuery(id+"F0.wireOp",EDGE,"E124"),sQuery(id+"F0.wireOp",EDGE,"E125"),sQuery(id+"F0.wireOp",EDGE,"E126"),sQuery(id+"F0.wireOp",EDGE,"E127"),sQuery(id+"F0.wireOp",EDGE,"E128"),sQuery(id+"F0.wireOp",EDGE,"E129"),sQuery(id+"F0.wireOp",EDGE,"E130")])],"isStart":false}),makeQuery(id+"F9.opExtrude","SWEPT_FACE",FACE,{"disambiguationData":[OSD([sQuery(id+"F8.wireOp",EDGE,"E135")])]})]});
            var sketch = newSketch(context, id + "F14", { "sketchPlane" : qUnion([Q0])});
            skLineSegment(sketch, "E158", {"start": v(4.94, 20.64) * mm, "end": v(6, 19.32) * mm});
            skLineSegment(sketch, "E159", {"start": v(6, 19.32) * mm, "end": v(7.62, 18.25) * mm});
            skLineSegment(sketch, "E160", {"start": v(7.62, 18.25) * mm, "end": v(8.96, 17.71) * mm});
            skLineSegment(sketch, "E161", {"start": v(8.96, 17.71) * mm, "end": v(9.12, 18.12) * mm});
            skLineSegment(sketch, "E162", {"start": v(9.12, 18.12) * mm, "end": v(7.87, 18.62) * mm});
            skLineSegment(sketch, "E163", {"start": v(7.87, 18.62) * mm, "end": v(6.48, 19.59) * mm});
            skLineSegment(sketch, "E164", {"start": v(6.48, 19.59) * mm, "end": v(5.54, 20.7) * mm});
            skLineSegment(sketch, "E165", {"start": v(5.54, 20.7) * mm, "end": v(5.54, 23.91) * mm});
            skLineSegment(sketch, "E166", {"start": v(5.54, 23.91) * mm, "end": v(4.97, 23.91) * mm});
            skLineSegment(sketch, "E167", {"start": v(4.94, 20.64) * mm, "end": v(4.97, 23.91) * mm});
            skSolve(sketch);
        }
        {
            var Q0;
            Q0 = qSketchRegion(id + "F14", true);
            extrude(context, id + "F15", {"entities" : qUnion([Q0]), "operationType" : NewBodyOperationType.ADD, "oppositeDirection" : true, "depth" : 7.62 * mm, "offsetDistance" : 25.4 * mm});
        }
        {
            var Q0;
            Q0=makeQuery(id+"F1.opExtrude","SWEPT_FACE",FACE,{"disambiguationData":[OSD([sQuery(id+"F0.wireOp",EDGE,"E39")])]});
            var sketch = newSketch(context, id + "F16", { "sketchPlane" : qUnion([Q0])});
            skCircle(sketch, "E168", {"center": v(3.66, 44.8) * mm, "radius": 1.1 * mm});
            skSolve(sketch);
        }
        {
            var Q0;
            Q0 = qSketchRegion(id + "F16", true);
            extrude(context, id + "F17", {"entities" : qUnion([Q0]), "operationType" : NewBodyOperationType.ADD, "depth" : 6.1 * mm, "offsetDistance" : 25.4 * mm});
        }
        {
            var Q0;
            Q0=makeQuery(id+"F17.opExtrude","CAP_FACE",FACE,{"disambiguationData":[OSD([sQuery(id+"F16.wireOp",EDGE,"E168")])],"isStart":false});
            var sketch = newSketch(context, id + "F18", { "sketchPlane" : qUnion([Q0])});
            skLineSegment(sketch, "E169.bottom", {"start": v(1.57, 45.88) * mm, "end": v(5.98, 45.88) * mm});
            skLineSegment(sketch, "E169.top", {"start": v(1.57, 43.69) * mm, "end": v(5.98, 43.69) * mm});
            skLineSegment(sketch, "E169.left", {"start": v(1.57, 45.88) * mm, "end": v(1.57, 43.69) * mm});
            skLineSegment(sketch, "E169.right", {"start": v(5.98, 45.88) * mm, "end": v(5.98, 43.69) * mm});
            skSolve(sketch);
        }
        {
            var Q0;
            Q0 = qSketchRegion(id + "F18", true);
            extrude(context, id + "F19", {"entities" : qUnion([Q0]), "operationType" : NewBodyOperationType.ADD, "depth" : 1.27 * mm, "offsetDistance" : 25.4 * mm});
        }
        {
            var Q0;
            Q0=makeQuery(id+"F15.boolean.opBoolean","MERGE",FACE,{"derivedFrom":[makeQuery(id+"F9.boolean.opBoolean","MERGE",FACE,{"derivedFrom":[makeQuery(id+"F1.opExtrude","CAP_FACE",FACE,{"disambiguationData":[OSD([sQuery(id+"F0.wireOp",EDGE,"E0"),sQuery(id+"F0.wireOp",EDGE,"E1"),sQuery(id+"F0.wireOp",EDGE,"E2"),sQuery(id+"F0.wireOp",EDGE,"E3"),sQuery(id+"F0.wireOp",EDGE,"E4"),sQuery(id+"F0.wireOp",EDGE,"E5"),sQuery(id+"F0.wireOp",EDGE,"E6"),sQuery(id+"F0.wireOp",EDGE,"E7"),sQuery(id+"F0.wireOp",EDGE,"E8"),sQuery(id+"F0.wireOp",EDGE,"E9"),sQuery(id+"F0.wireOp",EDGE,"E10"),sQuery(id+"F0.wireOp",EDGE,"E11"),sQuery(id+"F0.wireOp",EDGE,"E12"),sQuery(id+"F0.wireOp",EDGE,"E13"),sQuery(id+"F0.wireOp",EDGE,"E14"),sQuery(id+"F0.wireOp",EDGE,"E15"),sQuery(id+"F0.wireOp",EDGE,"E16"),sQuery(id+"F0.wireOp",EDGE,"E17"),sQuery(id+"F0.wireOp",EDGE,"E18"),sQuery(id+"F0.wireOp",EDGE,"E19"),sQuery(id+"F0.wireOp",EDGE,"E20"),sQuery(id+"F0.wireOp",EDGE,"E21"),sQuery(id+"F0.wireOp",EDGE,"E22"),sQuery(id+"F0.wireOp",EDGE,"E23"),sQuery(id+"F0.wireOp",EDGE,"E24"),sQuery(id+"F0.wireOp",EDGE,"E25"),sQuery(id+"F0.wireOp",EDGE,"E26"),sQuery(id+"F0.wireOp",EDGE,"E27"),sQuery(id+"F0.wireOp",EDGE,"E28"),sQuery(id+"F0.wireOp",EDGE,"E29"),sQuery(id+"F0.wireOp",EDGE,"E30"),sQuery(id+"F0.wireOp",EDGE,"E31"),sQuery(id+"F0.wireOp",EDGE,"E32"),sQuery(id+"F0.wireOp",EDGE,"E33"),sQuery(id+"F0.wireOp",EDGE,"E34"),sQuery(id+"F0.wireOp",EDGE,"E35"),sQuery(id+"F0.wireOp",EDGE,"E36"),sQuery(id+"F0.wireOp",EDGE,"E37"),sQuery(id+"F0.wireOp",EDGE,"E38"),sQuery(id+"F0.wireOp",EDGE,"E39"),sQuery(id+"F0.wireOp",EDGE,"E40"),sQuery(id+"F0.wireOp",EDGE,"E41"),sQuery(id+"F0.wireOp",EDGE,"E42"),sQuery(id+"F0.wireOp",EDGE,"E43"),sQuery(id+"F0.wireOp",EDGE,"E44"),sQuery(id+"F0.wireOp",EDGE,"E45"),sQuery(id+"F0.wireOp",EDGE,"E46"),sQuery(id+"F0.wireOp",EDGE,"E47"),sQuery(id+"F0.wireOp",EDGE,"E48"),sQuery(id+"F0.wireOp",EDGE,"E49"),sQuery(id+"F0.wireOp",EDGE,"E50"),sQuery(id+"F0.wireOp",EDGE,"E51"),sQuery(id+"F0.wireOp",EDGE,"E52"),sQuery(id+"F0.wireOp",EDGE,"E53"),sQuery(id+"F0.wireOp",EDGE,"E54"),sQuery(id+"F0.wireOp",EDGE,"E62"),sQuery(id+"F0.wireOp",EDGE,"E63"),sQuery(id+"F0.wireOp",EDGE,"E64"),sQuery(id+"F0.wireOp",EDGE,"E65"),sQuery(id+"F0.wireOp",EDGE,"E66"),sQuery(id+"F0.wireOp",EDGE,"E67"),sQuery(id+"F0.wireOp",EDGE,"E68"),sQuery(id+"F0.wireOp",EDGE,"E69"),sQuery(id+"F0.wireOp",EDGE,"E70"),sQuery(id+"F0.wireOp",EDGE,"E71"),sQuery(id+"F0.wireOp",EDGE,"E72"),sQuery(id+"F0.wireOp",EDGE,"E73"),sQuery(id+"F0.wireOp",EDGE,"E74"),sQuery(id+"F0.wireOp",EDGE,"E75"),sQuery(id+"F0.wireOp",EDGE,"E76"),sQuery(id+"F0.wireOp",EDGE,"E77"),sQuery(id+"F0.wireOp",EDGE,"E78"),sQuery(id+"F0.wireOp",EDGE,"E79"),sQuery(id+"F0.wireOp",EDGE,"E80"),sQuery(id+"F0.wireOp",EDGE,"E81"),sQuery(id+"F0.wireOp",EDGE,"E82"),sQuery(id+"F0.wireOp",EDGE,"E83"),sQuery(id+"F0.wireOp",EDGE,"E84"),sQuery(id+"F0.wireOp",EDGE,"E85"),sQuery(id+"F0.wireOp",EDGE,"E86"),sQuery(id+"F0.wireOp",EDGE,"E87"),sQuery(id+"F0.wireOp",EDGE,"E88"),sQuery(id+"F0.wireOp",EDGE,"E89"),sQuery(id+"F0.wireOp",EDGE,"E90"),sQuery(id+"F0.wireOp",EDGE,"E91"),sQuery(id+"F0.wireOp",EDGE,"E92"),sQuery(id+"F0.wireOp",EDGE,"E93"),sQuery(id+"F0.wireOp",EDGE,"E94"),sQuery(id+"F0.wireOp",EDGE,"E95"),sQuery(id+"F0.wireOp",EDGE,"E96"),sQuery(id+"F0.wireOp",EDGE,"E97"),sQuery(id+"F0.wireOp",EDGE,"E98"),sQuery(id+"F0.wireOp",EDGE,"E99"),sQuery(id+"F0.wireOp",EDGE,"E100"),sQuery(id+"F0.wireOp",EDGE,"E101"),sQuery(id+"F0.wireOp",EDGE,"E102"),sQuery(id+"F0.wireOp",EDGE,"E103"),sQuery(id+"F0.wireOp",EDGE,"E104"),sQuery(id+"F0.wireOp",EDGE,"E105"),sQuery(id+"F0.wireOp",EDGE,"E106"),sQuery(id+"F0.wireOp",EDGE,"E107"),sQuery(id+"F0.wireOp",EDGE,"E108"),sQuery(id+"F0.wireOp",EDGE,"E109"),sQuery(id+"F0.wireOp",EDGE,"E110"),sQuery(id+"F0.wireOp",EDGE,"E111"),sQuery(id+"F0.wireOp",EDGE,"E112"),sQuery(id+"F0.wireOp",EDGE,"E113"),sQuery(id+"F0.wireOp",EDGE,"E114"),sQuery(id+"F0.wireOp",EDGE,"E115"),sQuery(id+"F0.wireOp",EDGE,"E116"),sQuery(id+"F0.wireOp",EDGE,"E117"),sQuery(id+"F0.wireOp",EDGE,"E118"),sQuery(id+"F0.wireOp",EDGE,"E119"),sQuery(id+"F0.wireOp",EDGE,"E120"),sQuery(id+"F0.wireOp",EDGE,"E121.bottom"),sQuery(id+"F0.wireOp",EDGE,"E121.top"),sQuery(id+"F0.wireOp",EDGE,"E121.left"),sQuery(id+"F0.wireOp",EDGE,"E121.right"),sQuery(id+"F0.wireOp",EDGE,"E122"),sQuery(id+"F0.wireOp",EDGE,"E123"),sQuery(id+"F0.wireOp",EDGE,"E124"),sQuery(id+"F0.wireOp",EDGE,"E125"),sQuery(id+"F0.wireOp",EDGE,"E126"),sQuery(id+"F0.wireOp",EDGE,"E127"),sQuery(id+"F0.wireOp",EDGE,"E128"),sQuery(id+"F0.wireOp",EDGE,"E129"),sQuery(id+"F0.wireOp",EDGE,"E130")])],"isStart":false}),makeQuery(id+"F9.opExtrude","SWEPT_FACE",FACE,{"disambiguationData":[OSD([sQuery(id+"F8.wireOp",EDGE,"E135")])]})]}),makeQuery(id+"F15.opExtrude","CAP_FACE",FACE,{"disambiguationData":[OSD([sQuery(id+"F14.wireOp",EDGE,"E158"),sQuery(id+"F14.wireOp",EDGE,"E159"),sQuery(id+"F14.wireOp",EDGE,"E160"),sQuery(id+"F14.wireOp",EDGE,"E161"),sQuery(id+"F14.wireOp",EDGE,"E162"),sQuery(id+"F14.wireOp",EDGE,"E163"),sQuery(id+"F14.wireOp",EDGE,"E164"),sQuery(id+"F14.wireOp",EDGE,"E165"),sQuery(id+"F14.wireOp",EDGE,"E166"),sQuery(id+"F14.wireOp",EDGE,"E167")])],"isStart":true})]});
            var sketch = newSketch(context, id + "F20", { "sketchPlane" : qUnion([Q0])});
            skLineSegment(sketch, "E170", {"start": v(5.48, 33.54) * mm, "end": v(4.2, 31.5) * mm});
            skLineSegment(sketch, "E171", {"start": v(4.2, 31.5) * mm, "end": v(4.92, 31.05) * mm});
            skLineSegment(sketch, "E172", {"start": v(4.92, 31.05) * mm, "end": v(6.26, 33.19) * mm});
            skLineSegment(sketch, "E173", {"start": v(6.26, 33.19) * mm, "end": v(5.48, 33.54) * mm});
            skCircle(sketch, "E174", {"center": v(1.78, 30.83) * mm, "radius": 0.74 * mm});
            skLineSegment(sketch, "E175.bottom", {"start": v(4.92, 30.5) * mm, "end": v(6.16, 30.5) * mm});
            skLineSegment(sketch, "E175.top", {"start": v(4.92, 29.35) * mm, "end": v(6.16, 29.35) * mm});
            skLineSegment(sketch, "E175.left", {"start": v(4.92, 30.5) * mm, "end": v(4.92, 29.35) * mm});
            skLineSegment(sketch, "E175.right", {"start": v(6.16, 30.5) * mm, "end": v(6.16, 29.35) * mm});
            skSolve(sketch);
        }
        {
            var Q0;
            Q0=makeQuery(id+"F20.imprint","IMPRINT",FACE,{"disambiguationData":[TD([[makeQuery(id+"F20.imprint","IMPRINT",EDGE,{"derivedFrom":sQuery(id+"F20.wireOp",EDGE,"E170")}),1.0]])]});
            var Q1;
            Q1=makeQuery(id+"F20.imprint","IMPRINT",FACE,{"disambiguationData":[TD([[makeQuery(id+"F20.imprint","IMPRINT",EDGE,{"derivedFrom":sQuery(id+"F20.wireOp",EDGE,"E175.bottom")}),-1.0]])]});
            var Q2;
            Q2=makeQuery(id+"F20.imprint","IMPRINT",FACE,{"disambiguationData":[TD([[makeQuery(id+"F20.imprint","IMPRINT",EDGE,{"derivedFrom":sQuery(id+"F20.wireOp",EDGE,"E174")}),1.0]])]});
            var Q3;
            Q3=makeQuery(id+"F20.imprint","IMPRINT",FACE,{"disambiguationData":[TD([[makeQuery(id+"F20.imprint","IMPRINT",EDGE,{"derivedFrom":sQuery(id+"F20.wireOp",EDGE,"E170")}),-1.0]])]});
            extrude(context, id + "F21", {"entities" : qUnion([Q0, Q1, Q2, Q3]), "operationType" : NewBodyOperationType.ADD, "depth" : 0.5 * mm, "offsetDistance" : 25.4 * mm});
        }
        {
            var Q0;
            Q0=makeQuery(id+"F21.opExtrude","CAP_FACE",FACE,{"disambiguationData":[OSD([sQuery(id+"F0.wireOp",EDGE,"E0"),sQuery(id+"F0.wireOp",EDGE,"E1"),sQuery(id+"F0.wireOp",EDGE,"E2"),sQuery(id+"F0.wireOp",EDGE,"E3"),sQuery(id+"F0.wireOp",EDGE,"E4"),sQuery(id+"F0.wireOp",EDGE,"E5"),sQuery(id+"F0.wireOp",EDGE,"E6"),sQuery(id+"F0.wireOp",EDGE,"E7"),sQuery(id+"F0.wireOp",EDGE,"E8"),sQuery(id+"F0.wireOp",EDGE,"E9"),sQuery(id+"F0.wireOp",EDGE,"E10"),sQuery(id+"F0.wireOp",EDGE,"E11"),sQuery(id+"F0.wireOp",EDGE,"E12"),sQuery(id+"F0.wireOp",EDGE,"E13"),sQuery(id+"F0.wireOp",EDGE,"E14"),sQuery(id+"F0.wireOp",EDGE,"E15"),sQuery(id+"F0.wireOp",EDGE,"E16"),sQuery(id+"F0.wireOp",EDGE,"E17"),sQuery(id+"F0.wireOp",EDGE,"E18"),sQuery(id+"F0.wireOp",EDGE,"E19"),sQuery(id+"F0.wireOp",EDGE,"E20"),sQuery(id+"F0.wireOp",EDGE,"E21"),sQuery(id+"F0.wireOp",EDGE,"E22"),sQuery(id+"F0.wireOp",EDGE,"E23"),sQuery(id+"F0.wireOp",EDGE,"E24"),sQuery(id+"F0.wireOp",EDGE,"E25"),sQuery(id+"F0.wireOp",EDGE,"E26"),sQuery(id+"F0.wireOp",EDGE,"E27"),sQuery(id+"F0.wireOp",EDGE,"E28"),sQuery(id+"F0.wireOp",EDGE,"E29"),sQuery(id+"F0.wireOp",EDGE,"E30"),sQuery(id+"F0.wireOp",EDGE,"E31"),sQuery(id+"F0.wireOp",EDGE,"E32"),sQuery(id+"F0.wireOp",EDGE,"E33"),sQuery(id+"F0.wireOp",EDGE,"E34"),sQuery(id+"F0.wireOp",EDGE,"E35"),sQuery(id+"F0.wireOp",EDGE,"E36"),sQuery(id+"F0.wireOp",EDGE,"E37"),sQuery(id+"F0.wireOp",EDGE,"E38"),sQuery(id+"F0.wireOp",EDGE,"E39"),sQuery(id+"F0.wireOp",EDGE,"E40"),sQuery(id+"F0.wireOp",EDGE,"E41"),sQuery(id+"F0.wireOp",EDGE,"E42"),sQuery(id+"F0.wireOp",EDGE,"E43"),sQuery(id+"F0.wireOp",EDGE,"E44"),sQuery(id+"F0.wireOp",EDGE,"E45"),sQuery(id+"F0.wireOp",EDGE,"E46"),sQuery(id+"F0.wireOp",EDGE,"E47"),sQuery(id+"F0.wireOp",EDGE,"E48"),sQuery(id+"F0.wireOp",EDGE,"E49"),sQuery(id+"F0.wireOp",EDGE,"E50"),sQuery(id+"F0.wireOp",EDGE,"E51"),sQuery(id+"F0.wireOp",EDGE,"E52"),sQuery(id+"F0.wireOp",EDGE,"E53"),sQuery(id+"F0.wireOp",EDGE,"E54"),sQuery(id+"F0.wireOp",EDGE,"E62"),sQuery(id+"F0.wireOp",EDGE,"E63"),sQuery(id+"F0.wireOp",EDGE,"E64"),sQuery(id+"F0.wireOp",EDGE,"E65"),sQuery(id+"F0.wireOp",EDGE,"E66"),sQuery(id+"F0.wireOp",EDGE,"E67"),sQuery(id+"F0.wireOp",EDGE,"E68"),sQuery(id+"F0.wireOp",EDGE,"E69"),sQuery(id+"F0.wireOp",EDGE,"E70"),sQuery(id+"F0.wireOp",EDGE,"E71"),sQuery(id+"F0.wireOp",EDGE,"E72"),sQuery(id+"F0.wireOp",EDGE,"E73"),sQuery(id+"F0.wireOp",EDGE,"E74"),sQuery(id+"F0.wireOp",EDGE,"E75"),sQuery(id+"F0.wireOp",EDGE,"E76"),sQuery(id+"F0.wireOp",EDGE,"E77"),sQuery(id+"F0.wireOp",EDGE,"E78"),sQuery(id+"F0.wireOp",EDGE,"E79"),sQuery(id+"F0.wireOp",EDGE,"E80"),sQuery(id+"F0.wireOp",EDGE,"E81"),sQuery(id+"F0.wireOp",EDGE,"E82"),sQuery(id+"F0.wireOp",EDGE,"E83"),sQuery(id+"F0.wireOp",EDGE,"E84"),sQuery(id+"F0.wireOp",EDGE,"E85"),sQuery(id+"F0.wireOp",EDGE,"E86"),sQuery(id+"F0.wireOp",EDGE,"E87"),sQuery(id+"F0.wireOp",EDGE,"E88"),sQuery(id+"F0.wireOp",EDGE,"E89"),sQuery(id+"F0.wireOp",EDGE,"E90"),sQuery(id+"F0.wireOp",EDGE,"E91"),sQuery(id+"F0.wireOp",EDGE,"E92"),sQuery(id+"F0.wireOp",EDGE,"E93"),sQuery(id+"F0.wireOp",EDGE,"E94"),sQuery(id+"F0.wireOp",EDGE,"E95"),sQuery(id+"F0.wireOp",EDGE,"E96"),sQuery(id+"F0.wireOp",EDGE,"E97"),sQuery(id+"F0.wireOp",EDGE,"E98"),sQuery(id+"F0.wireOp",EDGE,"E99"),sQuery(id+"F0.wireOp",EDGE,"E100"),sQuery(id+"F0.wireOp",EDGE,"E101"),sQuery(id+"F0.wireOp",EDGE,"E102"),sQuery(id+"F0.wireOp",EDGE,"E103"),sQuery(id+"F0.wireOp",EDGE,"E104"),sQuery(id+"F0.wireOp",EDGE,"E105"),sQuery(id+"F0.wireOp",EDGE,"E106"),sQuery(id+"F0.wireOp",EDGE,"E107"),sQuery(id+"F0.wireOp",EDGE,"E108"),sQuery(id+"F0.wireOp",EDGE,"E109"),sQuery(id+"F0.wireOp",EDGE,"E110"),sQuery(id+"F0.wireOp",EDGE,"E111"),sQuery(id+"F0.wireOp",EDGE,"E112"),sQuery(id+"F0.wireOp",EDGE,"E113"),sQuery(id+"F0.wireOp",EDGE,"E114"),sQuery(id+"F0.wireOp",EDGE,"E115"),sQuery(id+"F0.wireOp",EDGE,"E116"),sQuery(id+"F0.wireOp",EDGE,"E117"),sQuery(id+"F0.wireOp",EDGE,"E118"),sQuery(id+"F0.wireOp",EDGE,"E119"),sQuery(id+"F0.wireOp",EDGE,"E120"),sQuery(id+"F0.wireOp",EDGE,"E121.bottom"),sQuery(id+"F0.wireOp",EDGE,"E121.top"),sQuery(id+"F0.wireOp",EDGE,"E121.left"),sQuery(id+"F0.wireOp",EDGE,"E121.right"),sQuery(id+"F0.wireOp",EDGE,"E122"),sQuery(id+"F0.wireOp",EDGE,"E123"),sQuery(id+"F0.wireOp",EDGE,"E124"),sQuery(id+"F0.wireOp",EDGE,"E125"),sQuery(id+"F0.wireOp",EDGE,"E126"),sQuery(id+"F0.wireOp",EDGE,"E127"),sQuery(id+"F0.wireOp",EDGE,"E128"),sQuery(id+"F0.wireOp",EDGE,"E129"),sQuery(id+"F0.wireOp",EDGE,"E130"),sQuery(id+"F8.wireOp",EDGE,"E135"),sQuery(id+"F8.wireOp",EDGE,"E136"),sQuery(id+"F10.wireOp",EDGE,"E138"),sQuery(id+"F10.wireOp",EDGE,"E139"),sQuery(id+"F14.wireOp",EDGE,"E158"),sQuery(id+"F14.wireOp",EDGE,"E159"),sQuery(id+"F14.wireOp",EDGE,"E160"),sQuery(id+"F14.wireOp",EDGE,"E161"),sQuery(id+"F14.wireOp",EDGE,"E162"),sQuery(id+"F14.wireOp",EDGE,"E163"),sQuery(id+"F14.wireOp",EDGE,"E164"),sQuery(id+"F14.wireOp",EDGE,"E165"),sQuery(id+"F14.wireOp",EDGE,"E167")])],"isStart":false});
            var sketch = newSketch(context, id + "F22", { "sketchPlane" : qUnion([Q0])});
            skLineSegment(sketch, "E176", {"start": v(-19.89, 38.06) * mm, "end": v(-19.89, 31.12) * mm});
            skLineSegment(sketch, "E177", {"start": v(-19.89, 31.12) * mm, "end": v(-19.1, 31.12) * mm});
            skLineSegment(sketch, "E178", {"start": v(-19.1, 31.12) * mm, "end": v(-19.1, 34.71) * mm});
            skLineSegment(sketch, "E179", {"start": v(-19.1, 34.71) * mm, "end": v(-17.34, 34.71) * mm});
            skLineSegment(sketch, "E180", {"start": v(-17.34, 34.71) * mm, "end": v(-17.34, 35.27) * mm});
            skLineSegment(sketch, "E181", {"start": v(-17.34, 35.27) * mm, "end": v(-18.97, 35.27) * mm});
            skLineSegment(sketch, "E182", {"start": v(-18.97, 35.27) * mm, "end": v(-18.97, 37.48) * mm});
            skLineSegment(sketch, "E183", {"start": v(-18.97, 37.48) * mm, "end": v(-16.62, 37.48) * mm});
            skLineSegment(sketch, "E184", {"start": v(-16.62, 37.48) * mm, "end": v(-16.62, 38.14) * mm});
            skLineSegment(sketch, "E185", {"start": v(-16.62, 38.14) * mm, "end": v(-19.89, 38.06) * mm});
            skLineSegment(sketch, "E186", {"start": v(-15.54, 38.14) * mm, "end": v(-15.54, 31.12) * mm});
            skLineSegment(sketch, "E187", {"start": v(-15.54, 31.12) * mm, "end": v(-14.92, 31.12) * mm});
            skLineSegment(sketch, "E188", {"start": v(-14.92, 31.12) * mm, "end": v(-14.92, 38.14) * mm});
            skLineSegment(sketch, "E189", {"start": v(-14.92, 38.14) * mm, "end": v(-15.54, 38.14) * mm});
            skSolve(sketch);
        }
        {
            var Q0;
            Q0 = qSketchRegion(id + "F22", true);
            extrude(context, id + "F23", {"entities" : qUnion([Q0]), "operationType" : NewBodyOperationType.REMOVE, "oppositeDirection" : true, "depth" : 1.02 * mm, "offsetDistance" : 25.4 * mm});
        }
        {
            var Q0;
            Q0=makeQuery(id+"F21.opExtrude","CAP_FACE",FACE,{"disambiguationData":[OSD([sQuery(id+"F0.wireOp",EDGE,"E0"),sQuery(id+"F0.wireOp",EDGE,"E1"),sQuery(id+"F0.wireOp",EDGE,"E2"),sQuery(id+"F0.wireOp",EDGE,"E3"),sQuery(id+"F0.wireOp",EDGE,"E4"),sQuery(id+"F0.wireOp",EDGE,"E5"),sQuery(id+"F0.wireOp",EDGE,"E6"),sQuery(id+"F0.wireOp",EDGE,"E7"),sQuery(id+"F0.wireOp",EDGE,"E8"),sQuery(id+"F0.wireOp",EDGE,"E9"),sQuery(id+"F0.wireOp",EDGE,"E10"),sQuery(id+"F0.wireOp",EDGE,"E11"),sQuery(id+"F0.wireOp",EDGE,"E12"),sQuery(id+"F0.wireOp",EDGE,"E13"),sQuery(id+"F0.wireOp",EDGE,"E14"),sQuery(id+"F0.wireOp",EDGE,"E15"),sQuery(id+"F0.wireOp",EDGE,"E16"),sQuery(id+"F0.wireOp",EDGE,"E17"),sQuery(id+"F0.wireOp",EDGE,"E18"),sQuery(id+"F0.wireOp",EDGE,"E19"),sQuery(id+"F0.wireOp",EDGE,"E20"),sQuery(id+"F0.wireOp",EDGE,"E21"),sQuery(id+"F0.wireOp",EDGE,"E22"),sQuery(id+"F0.wireOp",EDGE,"E23"),sQuery(id+"F0.wireOp",EDGE,"E24"),sQuery(id+"F0.wireOp",EDGE,"E25"),sQuery(id+"F0.wireOp",EDGE,"E26"),sQuery(id+"F0.wireOp",EDGE,"E27"),sQuery(id+"F0.wireOp",EDGE,"E28"),sQuery(id+"F0.wireOp",EDGE,"E29"),sQuery(id+"F0.wireOp",EDGE,"E30"),sQuery(id+"F0.wireOp",EDGE,"E31"),sQuery(id+"F0.wireOp",EDGE,"E32"),sQuery(id+"F0.wireOp",EDGE,"E33"),sQuery(id+"F0.wireOp",EDGE,"E34"),sQuery(id+"F0.wireOp",EDGE,"E35"),sQuery(id+"F0.wireOp",EDGE,"E36"),sQuery(id+"F0.wireOp",EDGE,"E37"),sQuery(id+"F0.wireOp",EDGE,"E38"),sQuery(id+"F0.wireOp",EDGE,"E39"),sQuery(id+"F0.wireOp",EDGE,"E40"),sQuery(id+"F0.wireOp",EDGE,"E41"),sQuery(id+"F0.wireOp",EDGE,"E42"),sQuery(id+"F0.wireOp",EDGE,"E43"),sQuery(id+"F0.wireOp",EDGE,"E44"),sQuery(id+"F0.wireOp",EDGE,"E45"),sQuery(id+"F0.wireOp",EDGE,"E46"),sQuery(id+"F0.wireOp",EDGE,"E47"),sQuery(id+"F0.wireOp",EDGE,"E48"),sQuery(id+"F0.wireOp",EDGE,"E49"),sQuery(id+"F0.wireOp",EDGE,"E50"),sQuery(id+"F0.wireOp",EDGE,"E51"),sQuery(id+"F0.wireOp",EDGE,"E52"),sQuery(id+"F0.wireOp",EDGE,"E53"),sQuery(id+"F0.wireOp",EDGE,"E54"),sQuery(id+"F0.wireOp",EDGE,"E62"),sQuery(id+"F0.wireOp",EDGE,"E63"),sQuery(id+"F0.wireOp",EDGE,"E64"),sQuery(id+"F0.wireOp",EDGE,"E65"),sQuery(id+"F0.wireOp",EDGE,"E66"),sQuery(id+"F0.wireOp",EDGE,"E67"),sQuery(id+"F0.wireOp",EDGE,"E68"),sQuery(id+"F0.wireOp",EDGE,"E69"),sQuery(id+"F0.wireOp",EDGE,"E70"),sQuery(id+"F0.wireOp",EDGE,"E71"),sQuery(id+"F0.wireOp",EDGE,"E72"),sQuery(id+"F0.wireOp",EDGE,"E73"),sQuery(id+"F0.wireOp",EDGE,"E74"),sQuery(id+"F0.wireOp",EDGE,"E75"),sQuery(id+"F0.wireOp",EDGE,"E76"),sQuery(id+"F0.wireOp",EDGE,"E77"),sQuery(id+"F0.wireOp",EDGE,"E78"),sQuery(id+"F0.wireOp",EDGE,"E79"),sQuery(id+"F0.wireOp",EDGE,"E80"),sQuery(id+"F0.wireOp",EDGE,"E81"),sQuery(id+"F0.wireOp",EDGE,"E82"),sQuery(id+"F0.wireOp",EDGE,"E83"),sQuery(id+"F0.wireOp",EDGE,"E84"),sQuery(id+"F0.wireOp",EDGE,"E85"),sQuery(id+"F0.wireOp",EDGE,"E86"),sQuery(id+"F0.wireOp",EDGE,"E87"),sQuery(id+"F0.wireOp",EDGE,"E88"),sQuery(id+"F0.wireOp",EDGE,"E89"),sQuery(id+"F0.wireOp",EDGE,"E90"),sQuery(id+"F0.wireOp",EDGE,"E91"),sQuery(id+"F0.wireOp",EDGE,"E92"),sQuery(id+"F0.wireOp",EDGE,"E93"),sQuery(id+"F0.wireOp",EDGE,"E94"),sQuery(id+"F0.wireOp",EDGE,"E95"),sQuery(id+"F0.wireOp",EDGE,"E96"),sQuery(id+"F0.wireOp",EDGE,"E97"),sQuery(id+"F0.wireOp",EDGE,"E98"),sQuery(id+"F0.wireOp",EDGE,"E99"),sQuery(id+"F0.wireOp",EDGE,"E100"),sQuery(id+"F0.wireOp",EDGE,"E101"),sQuery(id+"F0.wireOp",EDGE,"E102"),sQuery(id+"F0.wireOp",EDGE,"E103"),sQuery(id+"F0.wireOp",EDGE,"E104"),sQuery(id+"F0.wireOp",EDGE,"E105"),sQuery(id+"F0.wireOp",EDGE,"E106"),sQuery(id+"F0.wireOp",EDGE,"E107"),sQuery(id+"F0.wireOp",EDGE,"E108"),sQuery(id+"F0.wireOp",EDGE,"E109"),sQuery(id+"F0.wireOp",EDGE,"E110"),sQuery(id+"F0.wireOp",EDGE,"E111"),sQuery(id+"F0.wireOp",EDGE,"E112"),sQuery(id+"F0.wireOp",EDGE,"E113"),sQuery(id+"F0.wireOp",EDGE,"E114"),sQuery(id+"F0.wireOp",EDGE,"E115"),sQuery(id+"F0.wireOp",EDGE,"E116"),sQuery(id+"F0.wireOp",EDGE,"E117"),sQuery(id+"F0.wireOp",EDGE,"E118"),sQuery(id+"F0.wireOp",EDGE,"E119"),sQuery(id+"F0.wireOp",EDGE,"E120"),sQuery(id+"F0.wireOp",EDGE,"E121.bottom"),sQuery(id+"F0.wireOp",EDGE,"E121.top"),sQuery(id+"F0.wireOp",EDGE,"E121.left"),sQuery(id+"F0.wireOp",EDGE,"E121.right"),sQuery(id+"F0.wireOp",EDGE,"E122"),sQuery(id+"F0.wireOp",EDGE,"E123"),sQuery(id+"F0.wireOp",EDGE,"E124"),sQuery(id+"F0.wireOp",EDGE,"E125"),sQuery(id+"F0.wireOp",EDGE,"E126"),sQuery(id+"F0.wireOp",EDGE,"E127"),sQuery(id+"F0.wireOp",EDGE,"E128"),sQuery(id+"F0.wireOp",EDGE,"E129"),sQuery(id+"F0.wireOp",EDGE,"E130"),sQuery(id+"F8.wireOp",EDGE,"E135"),sQuery(id+"F8.wireOp",EDGE,"E136"),sQuery(id+"F10.wireOp",EDGE,"E138"),sQuery(id+"F10.wireOp",EDGE,"E139"),sQuery(id+"F14.wireOp",EDGE,"E158"),sQuery(id+"F14.wireOp",EDGE,"E159"),sQuery(id+"F14.wireOp",EDGE,"E160"),sQuery(id+"F14.wireOp",EDGE,"E161"),sQuery(id+"F14.wireOp",EDGE,"E162"),sQuery(id+"F14.wireOp",EDGE,"E163"),sQuery(id+"F14.wireOp",EDGE,"E164"),sQuery(id+"F14.wireOp",EDGE,"E165"),sQuery(id+"F14.wireOp",EDGE,"E167")])],"isStart":false});
            var sketch = newSketch(context, id + "F24", { "sketchPlane" : qUnion([Q0])});
            skLineSegment(sketch, "E190", {"start": v(18.61, 22.6) * mm, "end": v(23.5, 23.53) * mm});
            skLineSegment(sketch, "E191", {"start": v(23.5, 23.53) * mm, "end": v(32.29, -5.56) * mm});
            skLineSegment(sketch, "E192", {"start": v(32.29, -5.56) * mm, "end": v(27.57, -6.99) * mm});
            skLineSegment(sketch, "E193", {"start": v(27.57, -6.99) * mm, "end": v(18.61, 22.6) * mm});
            skSolve(sketch);
        }
        {
            var Q0;
            Q0 = qSketchRegion(id + "F24", true);
            extrude(context, id + "F25", {"entities" : qUnion([Q0]), "operationType" : NewBodyOperationType.REMOVE, "oppositeDirection" : true, "depth" : 1.02 * mm, "offsetDistance" : 25.4 * mm});
        }
        {
            var Q0;
            Q0=makeQuery(id+"F21.opExtrude","CAP_FACE",FACE,{"disambiguationData":[OSD([sQuery(id+"F0.wireOp",EDGE,"E0"),sQuery(id+"F0.wireOp",EDGE,"E1"),sQuery(id+"F0.wireOp",EDGE,"E2"),sQuery(id+"F0.wireOp",EDGE,"E3"),sQuery(id+"F0.wireOp",EDGE,"E4"),sQuery(id+"F0.wireOp",EDGE,"E5"),sQuery(id+"F0.wireOp",EDGE,"E6"),sQuery(id+"F0.wireOp",EDGE,"E7"),sQuery(id+"F0.wireOp",EDGE,"E8"),sQuery(id+"F0.wireOp",EDGE,"E9"),sQuery(id+"F0.wireOp",EDGE,"E10"),sQuery(id+"F0.wireOp",EDGE,"E11"),sQuery(id+"F0.wireOp",EDGE,"E12"),sQuery(id+"F0.wireOp",EDGE,"E13"),sQuery(id+"F0.wireOp",EDGE,"E14"),sQuery(id+"F0.wireOp",EDGE,"E15"),sQuery(id+"F0.wireOp",EDGE,"E16"),sQuery(id+"F0.wireOp",EDGE,"E17"),sQuery(id+"F0.wireOp",EDGE,"E18"),sQuery(id+"F0.wireOp",EDGE,"E19"),sQuery(id+"F0.wireOp",EDGE,"E20"),sQuery(id+"F0.wireOp",EDGE,"E21"),sQuery(id+"F0.wireOp",EDGE,"E22"),sQuery(id+"F0.wireOp",EDGE,"E23"),sQuery(id+"F0.wireOp",EDGE,"E24"),sQuery(id+"F0.wireOp",EDGE,"E25"),sQuery(id+"F0.wireOp",EDGE,"E26"),sQuery(id+"F0.wireOp",EDGE,"E27"),sQuery(id+"F0.wireOp",EDGE,"E28"),sQuery(id+"F0.wireOp",EDGE,"E29"),sQuery(id+"F0.wireOp",EDGE,"E30"),sQuery(id+"F0.wireOp",EDGE,"E31"),sQuery(id+"F0.wireOp",EDGE,"E32"),sQuery(id+"F0.wireOp",EDGE,"E33"),sQuery(id+"F0.wireOp",EDGE,"E34"),sQuery(id+"F0.wireOp",EDGE,"E35"),sQuery(id+"F0.wireOp",EDGE,"E36"),sQuery(id+"F0.wireOp",EDGE,"E37"),sQuery(id+"F0.wireOp",EDGE,"E38"),sQuery(id+"F0.wireOp",EDGE,"E39"),sQuery(id+"F0.wireOp",EDGE,"E40"),sQuery(id+"F0.wireOp",EDGE,"E41"),sQuery(id+"F0.wireOp",EDGE,"E42"),sQuery(id+"F0.wireOp",EDGE,"E43"),sQuery(id+"F0.wireOp",EDGE,"E44"),sQuery(id+"F0.wireOp",EDGE,"E45"),sQuery(id+"F0.wireOp",EDGE,"E46"),sQuery(id+"F0.wireOp",EDGE,"E47"),sQuery(id+"F0.wireOp",EDGE,"E48"),sQuery(id+"F0.wireOp",EDGE,"E49"),sQuery(id+"F0.wireOp",EDGE,"E50"),sQuery(id+"F0.wireOp",EDGE,"E51"),sQuery(id+"F0.wireOp",EDGE,"E52"),sQuery(id+"F0.wireOp",EDGE,"E53"),sQuery(id+"F0.wireOp",EDGE,"E54"),sQuery(id+"F0.wireOp",EDGE,"E62"),sQuery(id+"F0.wireOp",EDGE,"E63"),sQuery(id+"F0.wireOp",EDGE,"E64"),sQuery(id+"F0.wireOp",EDGE,"E65"),sQuery(id+"F0.wireOp",EDGE,"E66"),sQuery(id+"F0.wireOp",EDGE,"E67"),sQuery(id+"F0.wireOp",EDGE,"E68"),sQuery(id+"F0.wireOp",EDGE,"E69"),sQuery(id+"F0.wireOp",EDGE,"E70"),sQuery(id+"F0.wireOp",EDGE,"E71"),sQuery(id+"F0.wireOp",EDGE,"E72"),sQuery(id+"F0.wireOp",EDGE,"E73"),sQuery(id+"F0.wireOp",EDGE,"E74"),sQuery(id+"F0.wireOp",EDGE,"E75"),sQuery(id+"F0.wireOp",EDGE,"E76"),sQuery(id+"F0.wireOp",EDGE,"E77"),sQuery(id+"F0.wireOp",EDGE,"E78"),sQuery(id+"F0.wireOp",EDGE,"E79"),sQuery(id+"F0.wireOp",EDGE,"E80"),sQuery(id+"F0.wireOp",EDGE,"E81"),sQuery(id+"F0.wireOp",EDGE,"E82"),sQuery(id+"F0.wireOp",EDGE,"E83"),sQuery(id+"F0.wireOp",EDGE,"E84"),sQuery(id+"F0.wireOp",EDGE,"E85"),sQuery(id+"F0.wireOp",EDGE,"E86"),sQuery(id+"F0.wireOp",EDGE,"E87"),sQuery(id+"F0.wireOp",EDGE,"E88"),sQuery(id+"F0.wireOp",EDGE,"E89"),sQuery(id+"F0.wireOp",EDGE,"E90"),sQuery(id+"F0.wireOp",EDGE,"E91"),sQuery(id+"F0.wireOp",EDGE,"E92"),sQuery(id+"F0.wireOp",EDGE,"E93"),sQuery(id+"F0.wireOp",EDGE,"E94"),sQuery(id+"F0.wireOp",EDGE,"E95"),sQuery(id+"F0.wireOp",EDGE,"E96"),sQuery(id+"F0.wireOp",EDGE,"E97"),sQuery(id+"F0.wireOp",EDGE,"E98"),sQuery(id+"F0.wireOp",EDGE,"E99"),sQuery(id+"F0.wireOp",EDGE,"E100"),sQuery(id+"F0.wireOp",EDGE,"E101"),sQuery(id+"F0.wireOp",EDGE,"E102"),sQuery(id+"F0.wireOp",EDGE,"E103"),sQuery(id+"F0.wireOp",EDGE,"E104"),sQuery(id+"F0.wireOp",EDGE,"E105"),sQuery(id+"F0.wireOp",EDGE,"E106"),sQuery(id+"F0.wireOp",EDGE,"E107"),sQuery(id+"F0.wireOp",EDGE,"E108"),sQuery(id+"F0.wireOp",EDGE,"E109"),sQuery(id+"F0.wireOp",EDGE,"E110"),sQuery(id+"F0.wireOp",EDGE,"E111"),sQuery(id+"F0.wireOp",EDGE,"E112"),sQuery(id+"F0.wireOp",EDGE,"E113"),sQuery(id+"F0.wireOp",EDGE,"E114"),sQuery(id+"F0.wireOp",EDGE,"E115"),sQuery(id+"F0.wireOp",EDGE,"E116"),sQuery(id+"F0.wireOp",EDGE,"E117"),sQuery(id+"F0.wireOp",EDGE,"E118"),sQuery(id+"F0.wireOp",EDGE,"E119"),sQuery(id+"F0.wireOp",EDGE,"E120"),sQuery(id+"F0.wireOp",EDGE,"E121.bottom"),sQuery(id+"F0.wireOp",EDGE,"E121.top"),sQuery(id+"F0.wireOp",EDGE,"E121.left"),sQuery(id+"F0.wireOp",EDGE,"E121.right"),sQuery(id+"F0.wireOp",EDGE,"E122"),sQuery(id+"F0.wireOp",EDGE,"E123"),sQuery(id+"F0.wireOp",EDGE,"E124"),sQuery(id+"F0.wireOp",EDGE,"E125"),sQuery(id+"F0.wireOp",EDGE,"E126"),sQuery(id+"F0.wireOp",EDGE,"E127"),sQuery(id+"F0.wireOp",EDGE,"E128"),sQuery(id+"F0.wireOp",EDGE,"E129"),sQuery(id+"F0.wireOp",EDGE,"E130"),sQuery(id+"F8.wireOp",EDGE,"E135"),sQuery(id+"F8.wireOp",EDGE,"E136"),sQuery(id+"F10.wireOp",EDGE,"E138"),sQuery(id+"F10.wireOp",EDGE,"E139"),sQuery(id+"F14.wireOp",EDGE,"E158"),sQuery(id+"F14.wireOp",EDGE,"E159"),sQuery(id+"F14.wireOp",EDGE,"E160"),sQuery(id+"F14.wireOp",EDGE,"E161"),sQuery(id+"F14.wireOp",EDGE,"E162"),sQuery(id+"F14.wireOp",EDGE,"E163"),sQuery(id+"F14.wireOp",EDGE,"E164"),sQuery(id+"F14.wireOp",EDGE,"E165"),sQuery(id+"F14.wireOp",EDGE,"E167")])],"isStart":false});
            var sketch = newSketch(context, id + "F26", { "sketchPlane" : qUnion([Q0])});
            skLineSegment(sketch, "E194", {"start": v(-45.03, 33.39) * mm, "end": v(-45.03, 13.89) * mm});
            skLineSegment(sketch, "E195", {"start": v(-45.03, 13.89) * mm, "end": v(-28.06, 29.22) * mm});
            skLineSegment(sketch, "E196", {"start": v(-28.06, 29.22) * mm, "end": v(-45.03, 33.39) * mm});
            skSolve(sketch);
        }
        {
            var Q0;
            Q0 = qSketchRegion(id + "F26", true);
            extrude(context, id + "F27", {"entities" : qUnion([Q0]), "operationType" : NewBodyOperationType.REMOVE, "oppositeDirection" : true, "depth" : 25.4 * mm, "offsetDistance" : 25.4 * mm});
        }
    });
